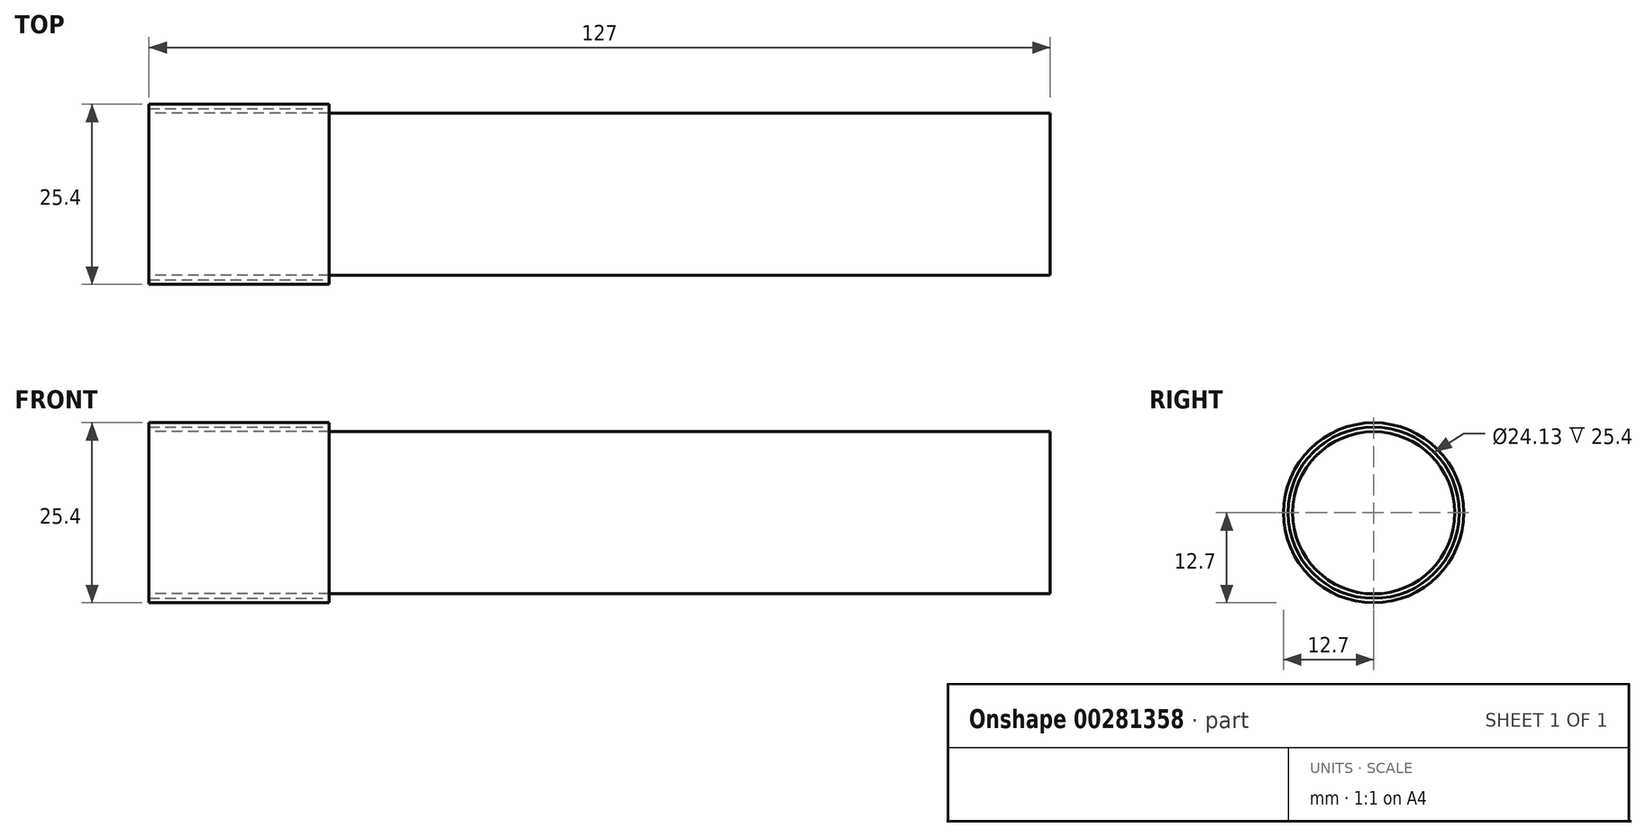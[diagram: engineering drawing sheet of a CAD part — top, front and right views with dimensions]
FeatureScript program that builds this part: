
annotation { "Feature Type Name" : "Feature", "Feature Type Description" : "" }
export const myFeature = defineFeature(function(context is Context, id is Id, definition is map)
    precondition{}
    {
        {
            var Q0;
            Q0=qCreatedBy(makeId("Right.planeOp"),FACE);
            var sketch = newSketch(context, id + "F0", { "sketchPlane" : qUnion([Q0])});
            skCircle(sketch, "E0", {"center": v(0, 0) * mm, "radius": 12.7 * mm});
            skSolve(sketch);
        }
        {
            var Q0;
            Q0=makeQuery(id+"F0.imprint","IMPRINT",FACE,{"disambiguationData":[TD([[makeQuery(id+"F0.imprint","IMPRINT",EDGE,{"derivedFrom":sQuery(id+"F0.wireOp",EDGE,"E0")}),1.0]])]});
            extrude(context, id + "F1", {"entities" : qUnion([Q0]), "depth" : 25.4 * mm});
        }
        {
            var Q0;
            Q0=makeQuery(id+"F1.opExtrude","CAP_FACE",FACE,{"disambiguationData":[OSD([sQuery(id+"F0.wireOp",EDGE,"E0")])],"isStart":false});
            var sketch = newSketch(context, id + "F2", { "sketchPlane" : qUnion([Q0])});
            skPoint(sketch, "E1", {"position": v(0, 0) * mm});
            skSolve(sketch);
        }
        {
            var Q0;
            Q0=sQuery(id+"F2.wireOp",VERTEX,"E1");
            var Q1;
            Q1=makeQuery(id+"F1.opExtrude","SWEPT_BODY",BODY,{"disambiguationData":[OSD([sQuery(id+"F0.wireOp",EDGE,"E0")])]});
            hole(context, id + "F3", {"style" : HoleStyle.SIMPLE, "endStyle" : HoleEndStyle.THROUGH, "holeDiameter" : 24.13 * mm, "tappedDepth" : 76.2 * mm, "tapClearance" : 3, "startFromSketch" : true, "locations" : qUnion([Q0]), "scope" : qUnion([Q1])});
        }
        {
            var Q0;
            Q0=qCreatedBy(makeId("Right.planeOp"),FACE);
            var sketch = newSketch(context, id + "F4", { "sketchPlane" : qUnion([Q0])});
            skCircle(sketch, "E2", {"center": v(0, 0) * mm, "radius": 11.43 * mm});
            skSolve(sketch);
        }
        {
            var Q0;
            Q0=makeQuery(id+"F4.imprint","IMPRINT",FACE,{"disambiguationData":[TD([[makeQuery(id+"F4.imprint","IMPRINT",EDGE,{"derivedFrom":sQuery(id+"F4.wireOp",EDGE,"E2")}),1.0]])]});
            extrude(context, id + "F5", {"entities" : qUnion([Q0]), "depth" : 127 * mm});
        }
        {
            var Q0;
            Q0=qCreatedBy(makeId("Top.planeOp"),FACE);
            var sketch = newSketch(context, id + "F6", { "sketchPlane" : qUnion([Q0])});
            skCircle(sketch, "E3", {"center": v(38.47, 0) * mm, "radius": 4.78 * mm});
            skSolve(sketch);
        }
        {
            var Q0;
            Q0=sQuery(id+"F6.wireOp",EDGE,"E3");
            extrude(context, id + "F7", {"bodyType" : ToolBodyType.SURFACE, "operationType" : NewBodyOperationType.ADD, "flatOperationType" : FlatOperationType.REMOVE, "surfaceEntities" : qUnion([Q0]), "offsetDistance" : 25.4 * mm, "depth" : 16.1 * mm, "hasSecondDirection" : true, "secondDirectionOppositeDirection" : true, "secondDirectionDepth" : 15.38 * mm, "domain" : OperationDomain.MODEL});
        }
    });
